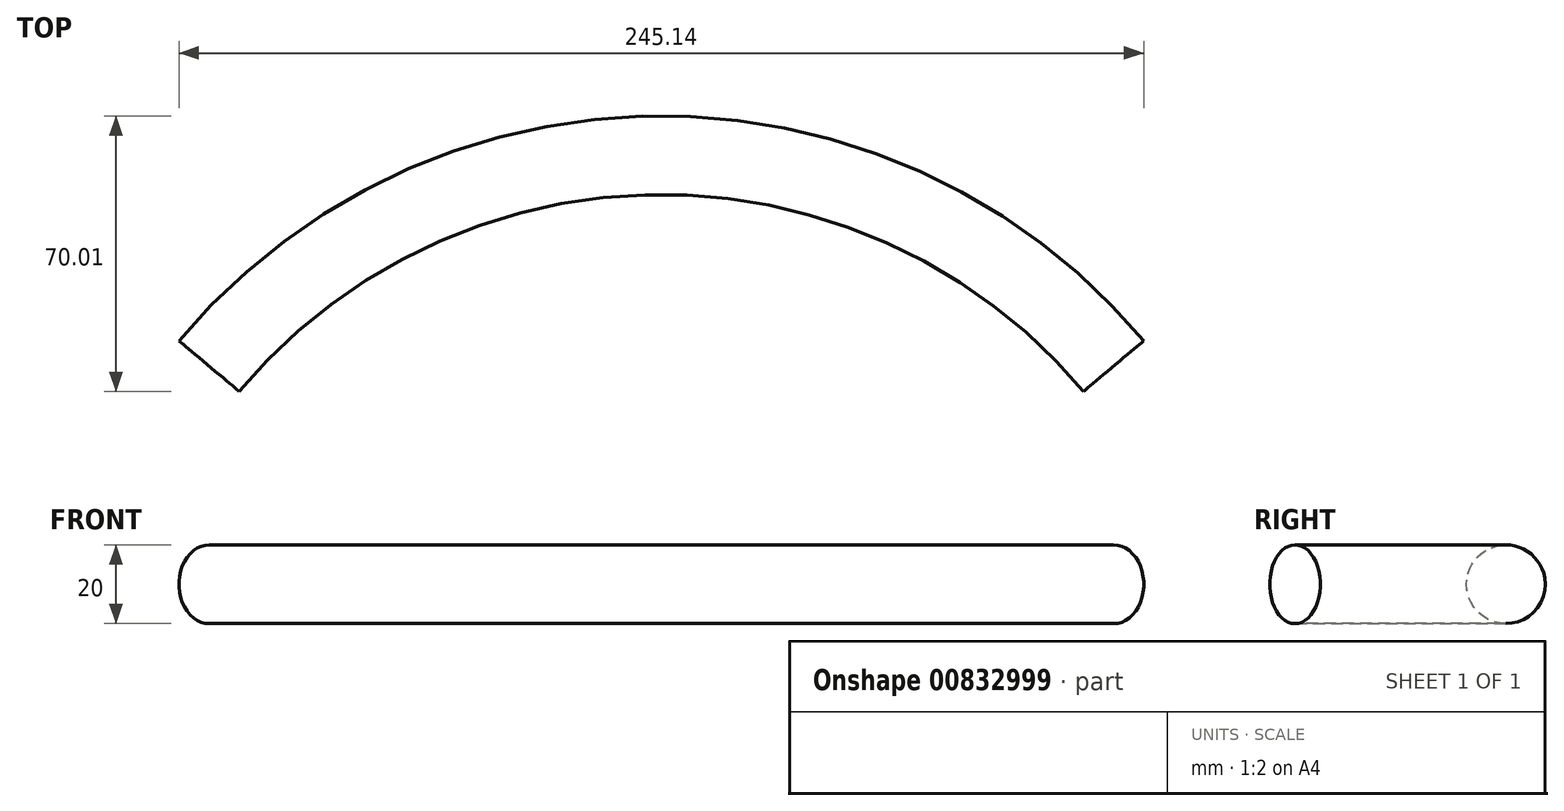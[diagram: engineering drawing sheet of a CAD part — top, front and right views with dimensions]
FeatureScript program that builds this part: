
annotation { "Feature Type Name" : "Feature", "Feature Type Description" : "" }
export const myFeature = defineFeature(function(context is Context, id is Id, definition is map)
    precondition{}
    {
        {
            var Q0;
            Q0=qCreatedBy(makeId("Right.planeOp"),FACE);
            var sketch = newSketch(context, id + "F0", { "sketchPlane" : qUnion([Q0])});
            skCircle(sketch, "E0", {"center": v(0, 0) * mm, "radius": 10 * mm});
            skLineSegment(sketch, "E1", {"start": v(-150, 19.5) * mm, "end": v(-150, -18.24) * mm});
            skSolve(sketch);
        }
        {
            var Q0;
            Q0=makeQuery(id+"F0.imprint","IMPRINT",FACE,{"disambiguationData":[TD([[makeQuery(id+"F0.imprint","IMPRINT",EDGE,{"derivedFrom":sQuery(id+"F0.wireOp",EDGE,"E0")}),1.0]])]});
            var Q1;
            Q1=sQuery(id+"F0.wireOp",EDGE,"E1");
            revolve(context, id + "F1", {"surfaceOperationType" : NewSurfaceOperationType.NEW, "entities" : qUnion([Q0]), "axis" : qUnion([Q1]), "revolveType" : RevolveType.SYMMETRIC, "angle" : 100 * degree});
        }
    });
